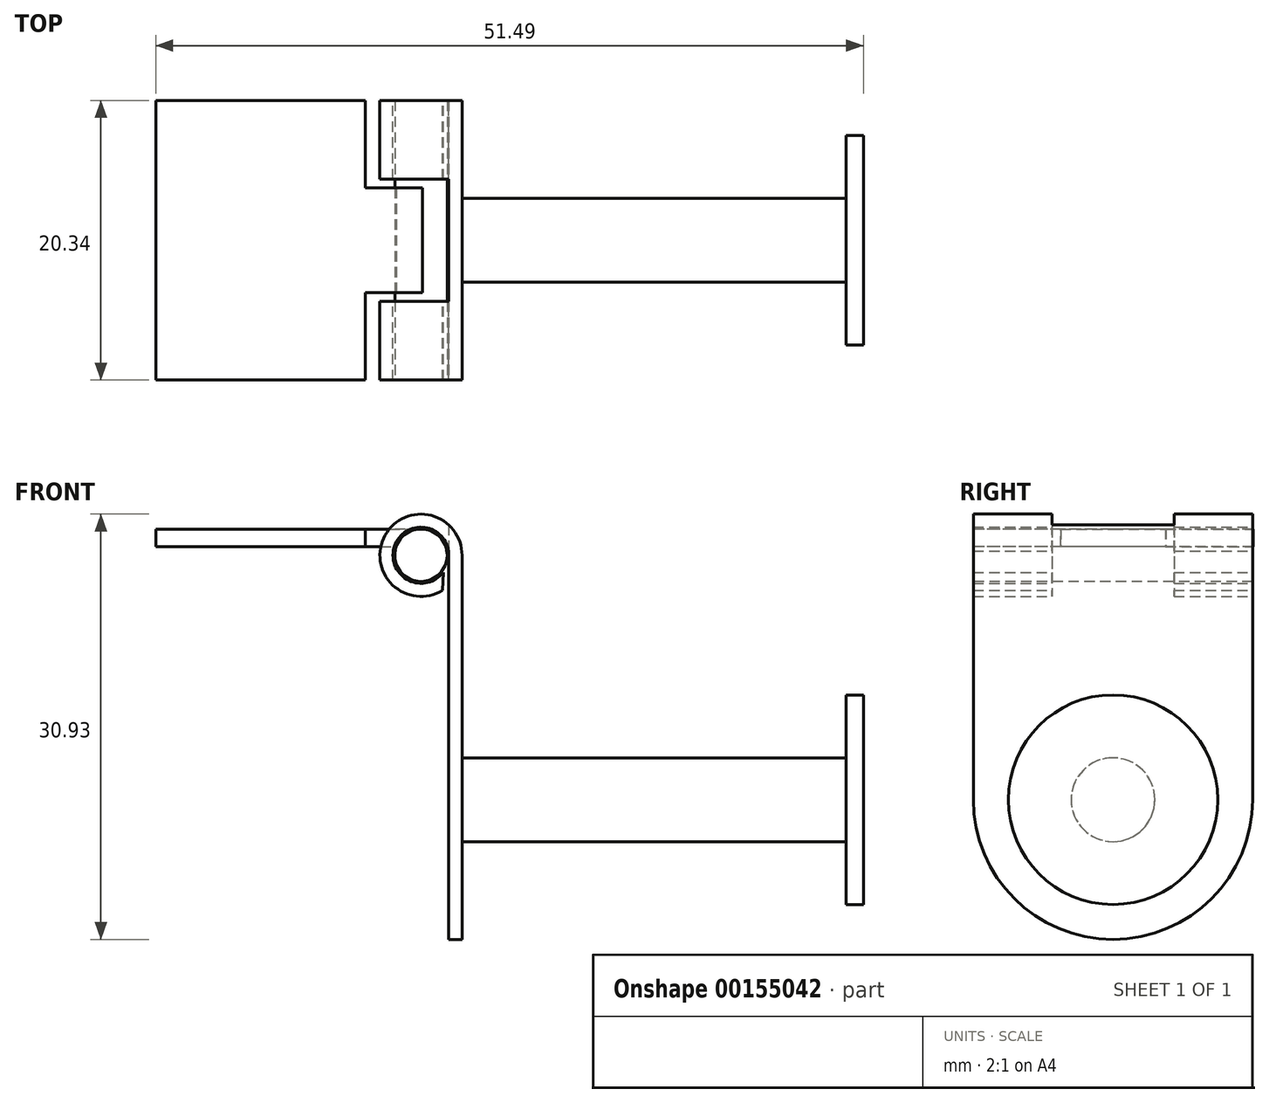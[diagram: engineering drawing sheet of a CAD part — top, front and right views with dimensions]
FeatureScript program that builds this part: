
annotation { "Feature Type Name" : "Feature", "Feature Type Description" : "" }
export const myFeature = defineFeature(function(context is Context, id is Id, definition is map)
    precondition{}
    {
        {
            var Q0;
            Q0=qCreatedBy(makeId("Front.planeOp"),FACE);
            var sketch = newSketch(context, id + "F0", { "sketchPlane" : qUnion([Q0])});
            skLineSegment(sketch, "E0", {"start": v(0, 0) * mm, "end": v(0, 28.26) * mm});
            skLineSegment(sketch, "E1", {"start": v(0, 0) * mm, "end": v(0.98, 0) * mm});
            skLineSegment(sketch, "E2", {"start": v(0.98, 0) * mm, "end": v(0.98, 27.94) * mm});
            skArc(sketch, "E3", {"start": v(0.98, 27.94) * mm, "mid": v(-4.62, 29.4) * mm, "end": v(-0.45, 25.4) * mm});
            skArc(sketch, "E4", {"start": v(0, 28.26) * mm, "mid": v(-3.99, 28.44) * mm, "end": v(-0.4, 26.7) * mm});
            skLineSegment(sketch, "E5", {"start": v(-0.4, 26.7) * mm, "end": v(-0.45, 25.4) * mm});
            skSolve(sketch);
        }
        {
            var Q0;
            Q0 = qSketchRegion(id + "F0", true);
            extrude(context, id + "F1", {"entities" : qUnion([Q0]), "depth" : 20.32 * mm});
        }
        {
            var Q0;
            Q0=makeQuery(id+"F1.opExtrude","SWEPT_FACE",FACE,{"disambiguationData":[OSD([sQuery(id+"F0.wireOp",EDGE,"E1")])]});
            var sketch = newSketch(context, id + "F2", { "sketchPlane" : qUnion([Q0])});
            skLineSegment(sketch, "E6", {"start": v(0, 10.16) * mm, "end": v(-6.64, 10.16) * mm});
            skLineSegment(sketch, "E7.bottom", {"start": v(0, 5.72) * mm, "end": v(-8.35, 5.72) * mm});
            skLineSegment(sketch, "E7.top", {"start": v(0, 14.6) * mm, "end": v(-8.35, 14.6) * mm});
            skLineSegment(sketch, "E7.left", {"start": v(0, 5.72) * mm, "end": v(0, 14.6) * mm});
            skLineSegment(sketch, "E7.right", {"start": v(-8.35, 5.72) * mm, "end": v(-8.35, 14.6) * mm});
            skLineSegment(sketch, "E8", {"start": v(-6.64, 10.16) * mm, "end": v(-6.64, 5.72) * mm});
            skLineSegment(sketch, "E9", {"start": v(-6.64, 10.16) * mm, "end": v(-6.64, 14.6) * mm});
            skSolve(sketch);
        }
        {
            var Q0;
            Q0 = qSketchRegion(id + "F2", true);
            extrude(context, id + "F3", {"entities" : qUnion([Q0]), "operationType" : NewBodyOperationType.REMOVE, "oppositeDirection" : true, "depth" : 50.8 * mm});
        }
        {
            var Q0;
            Q0=makeQuery(id+"F1.opExtrude","CAP_FACE",FACE,{"disambiguationData":[OSD([sQuery(id+"F0.wireOp",EDGE,"E0"),sQuery(id+"F0.wireOp",EDGE,"E1"),sQuery(id+"F0.wireOp",EDGE,"E2"),sQuery(id+"F0.wireOp",EDGE,"E3"),sQuery(id+"F0.wireOp",EDGE,"E4"),sQuery(id+"F0.wireOp",EDGE,"E5")])],"isStart":false});
            var sketch = newSketch(context, id + "F4", { "sketchPlane" : qUnion([Q0])});
            skCircle(sketch, "E10", {"center": v(-2.01, 27.94) * mm, "radius": 1.9 * mm});
            skPoint(sketch, "E11", {"position": v(-2.01, 29.85) * mm});
            skSolve(sketch);
        }
        {
            var Q0;
            Q0 = qSketchRegion(id + "F4", true);
            extrude(context, id + "F5", {"entities" : qUnion([Q0]), "operationType" : NewBodyOperationType.ADD, "oppositeDirection" : true, "depth" : 20.32 * mm});
        }
        {
            var Q0;
            Q0=qCreatedBy(makeId("Top.planeOp"),FACE);
            cPlane(context, id + "F6", {"entities" : qUnion([Q0]), "cplaneType" : CPlaneType.OFFSET, "offset" : 28.57 * mm, "width" : 152.4 * mm, "height" : 152.4 * mm});
        }
        {
            var Q0;
            Q0=qCreatedBy(id+"F6.planeOp",FACE);
            var sketch = newSketch(context, id + "F7", { "sketchPlane" : qUnion([Q0])});
            skLineSegment(sketch, "E12", {"start": v(-6.06, -13.97) * mm, "end": v(-1.9, -13.97) * mm});
            skLineSegment(sketch, "E13", {"start": v(-1.9, -6.35) * mm, "end": v(-6.06, -6.33) * mm});
            skPoint(sketch, "E14", {"position": v(-1.9, -10.16) * mm});
            skLineSegment(sketch, "E15", {"start": v(-1.9, -10.16) * mm, "end": v(-1.9, -13.97) * mm});
            skLineSegment(sketch, "E16", {"start": v(-1.9, -10.16) * mm, "end": v(-1.9, -6.35) * mm});
            skLineSegment(sketch, "E17", {"start": v(-6.06, -6.33) * mm, "end": v(-6.06, 0.02) * mm});
            skLineSegment(sketch, "E18", {"start": v(-6.06, 0.02) * mm, "end": v(-21.3, 0.02) * mm});
            skLineSegment(sketch, "E19", {"start": v(-21.3, 0.02) * mm, "end": v(-21.3, -20.3) * mm});
            skLineSegment(sketch, "E20", {"start": v(-6.06, -13.97) * mm, "end": v(-6.06, -20.32) * mm});
            skLineSegment(sketch, "E21", {"start": v(0, 0) * mm, "end": v(0, -10.16) * mm});
            skLineSegment(sketch, "E22", {"start": v(0, -10.16) * mm, "end": v(-1.9, -10.16) * mm});
            skLineSegment(sketch, "E23", {"start": v(-6.06, -20.32) * mm, "end": v(-21.3, -20.3) * mm});
            skLineSegment(sketch, "E24", {"start": v(-6.06, -6.33) * mm, "end": v(-6.06, -13.97) * mm});
            skSolve(sketch);
        }
        {
            var Q0;
            Q0 = qSketchRegion(id + "F7", true);
            extrude(context, id + "F8", {"entities" : qUnion([Q0]), "operationType" : NewBodyOperationType.ADD, "depth" : 1.27 * mm});
        }
        {
            var Q0;
            Q0=makeQuery(id+"F1.opExtrude","CAP_EDGE",EDGE,{"disambiguationData":[OSD([sQuery(id+"F0.wireOp",EDGE,"E1")])],"isStart":true});
            var Q1;
            Q1=makeQuery(id+"F1.opExtrude","CAP_EDGE",EDGE,{"disambiguationData":[OSD([sQuery(id+"F0.wireOp",EDGE,"E1")])],"isStart":false});
            fillet(context, id + "F9", {"entities" : qUnion([Q0, Q1]), "radius" : 10.16 * mm, "tangentPropagation" : true, "allowEdgeOverflow" : false});
        }
        {
            var Q0;
            Q0=makeQuery(id+"F1.opExtrude","SWEPT_FACE",FACE,{"disambiguationData":[OSD([sQuery(id+"F0.wireOp",EDGE,"E2")])]});
            var sketch = newSketch(context, id + "F10", { "sketchPlane" : qUnion([Q0])});
            skCircle(sketch, "E25", {"center": v(-10.16, 10.16) * mm, "radius": 3.05 * mm});
            skSolve(sketch);
        }
        {
            var Q0;
            Q0 = qSketchRegion(id + "F10", true);
            extrude(context, id + "F11", {"entities" : qUnion([Q0]), "operationType" : NewBodyOperationType.ADD, "depth" : 27.94 * mm});
        }
        {
            var Q0;
            Q0=makeQuery(id+"F11.opExtrude","CAP_FACE",FACE,{"disambiguationData":[OSD([sQuery(id+"F10.wireOp",EDGE,"E25")])],"isStart":false});
            var sketch = newSketch(context, id + "F12", { "sketchPlane" : qUnion([Q0])});
            skCircle(sketch, "E26", {"center": v(-10.16, 10.16) * mm, "radius": 7.62 * mm});
            skSolve(sketch);
        }
        {
            var Q0;
            Q0 = qSketchRegion(id + "F12", true);
            extrude(context, id + "F13", {"entities" : qUnion([Q0]), "operationType" : NewBodyOperationType.ADD, "depth" : 1.27 * mm});
        }
    });
